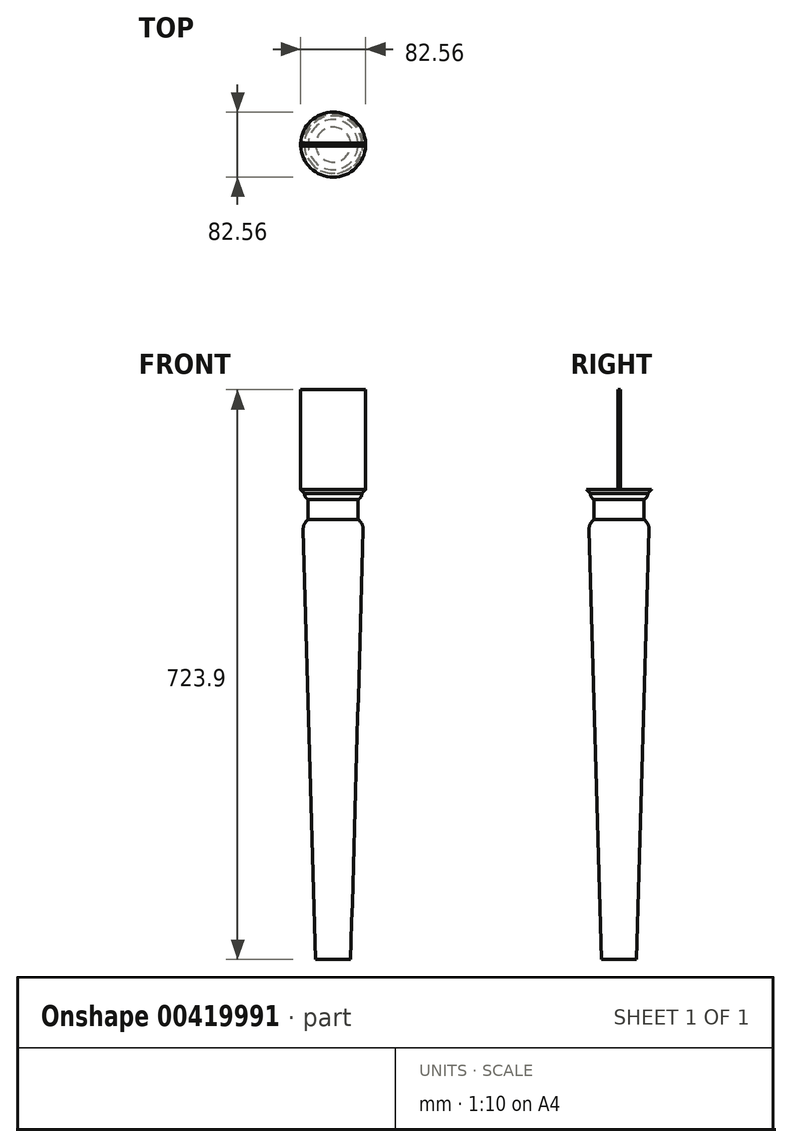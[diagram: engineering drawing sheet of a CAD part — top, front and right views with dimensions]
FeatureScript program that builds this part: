
annotation { "Feature Type Name" : "Feature", "Feature Type Description" : "" }
export const myFeature = defineFeature(function(context is Context, id is Id, definition is map)
    precondition{}
    {
        {
            assignVariable(context, id + "F0", {"name" : "squareSize", "anyValue" : 3.25});
        }
        {
            var Q0;
            Q0=qCreatedBy(makeId("Front.planeOp"),FACE);
            var sketch = newSketch(context, id + "F1", { "sketchPlane" : qUnion([Q0])});
            skLineSegment(sketch, "E0", {"start": v(0, 0) * mm, "end": v(0, -723.9) * mm});
            skLineSegment(sketch, "E1", {"start": v(0, 0) * mm, "end": v(41.27, 0) * mm});
            skLineSegment(sketch, "E2", {"start": v(41.27, 0) * mm, "end": v(41.28, -127) * mm});
            skLineSegment(sketch, "E3", {"start": v(22.23, -723.9) * mm, "end": v(38.1, -177.8) * mm});
            skLineSegment(sketch, "E4", {"start": v(41.27, -127) * mm, "end": v(0, -127) * mm});
            skLineSegment(sketch, "E5", {"start": v(41.28, -127) * mm, "end": v(41.28, -723.9) * mm, "construction": true});
            skLineSegment(sketch, "E6.MirrorCS", {"start": v(-41.27, -127) * mm, "end": v(0, -127) * mm});
            skLineSegment(sketch, "E7.MirrorCS", {"start": v(-41.27, 0) * mm, "end": v(-41.28, -127) * mm});
            skLineSegment(sketch, "E8.MirrorCS", {"start": v(0, 0) * mm, "end": v(-41.27, 0) * mm});
            skLineSegment(sketch, "E9", {"start": v(31.75, -139.7) * mm, "end": v(31.75, -165.1) * mm});
            skArc(sketch, "E10", {"start": v(36.51, -131.76) * mm, "mid": v(53.34, -112.03) * mm, "end": v(65.6, -89.16) * mm});
            skArc(sketch, "E11", {"start": v(31.75, -139.7) * mm, "mid": v(35.23, -136.4) * mm, "end": v(36.51, -131.76) * mm});
            skArc(sketch, "E12", {"start": v(38.1, -177.8) * mm, "mid": v(36.52, -170.65) * mm, "end": v(31.75, -165.1) * mm});
            skLineSegment(sketch, "E13", {"start": v(22.23, -723.9) * mm, "end": v(0, -723.9) * mm});
            skLineSegment(sketch, "E14", {"start": v(-41.27, -89.16) * mm, "end": v(65.6, -89.16) * mm});
            skPoint(sketch, "E15.orphan", {"position": v(0, -89.16) * mm});
            skSolve(sketch);
        }
        {
            var Q0;
            Q0=makeQuery(id+"F1.imprint","IMPRINT",FACE,{"disambiguationData":[TD([[makeQuery(id+"F1.imprint","IMPRINT",EDGE,{"derivedFrom":sQuery(id+"F1.wireOp",EDGE,"E1")}),-1.0]])]});
            var Q1;
            {var subQ2=sQuery(id+"F1.wireOp",EDGE,"E6.MirrorCS");Q1=makeQuery(id+"F1.imprint","IMPRINT",FACE,{"disambiguationData":[TD([[makeQuery(id+"F1.imprint","IMPRINT",EDGE,{"derivedFrom":subQ2}),1.0]])]});}
            var Q2;
            {var subQ0=sQuery(id+"F1.wireOp",EDGE,"E4");Q2=makeQuery(id+"F1.imprint","IMPRINT",FACE,{"disambiguationData":[TD([[makeQuery(id+"F1.imprint","IMPRINT",EDGE,{"derivedFrom":subQ0}),-1.0]])]});}
            extrude(context, id + "F2", {"entities" : qUnion([Q0, Q1, Q2]), "endBound" : BoundingType.SYMMETRIC, "depth" : (getVariable(context, 'squareSize')) * mm});
        }
        {
            var Q0;
            Q0=makeQuery(id+"F1.imprint","IMPRINT",FACE,{"disambiguationData":[TD([[makeQuery(id+"F1.imprint","IMPRINT",EDGE,{"derivedFrom":sQuery(id+"F1.wireOp",EDGE,"E3")}),1.0]])]});
            var Q1;
            {var subQ0=sQuery(id+"F1.wireOp",EDGE,"E4");Q1=makeQuery(id+"F1.imprint","IMPRINT",FACE,{"disambiguationData":[TD([[makeQuery(id+"F1.imprint","IMPRINT",EDGE,{"derivedFrom":subQ0}),-1.0]])]});}
            var Q2;
            {var subQ0=sQuery(id+"F1.wireOp",EDGE,"E10");var subQ3=sQuery(id+"F1.wireOp",EDGE,"E14");var subQ5=makeQuery(id+"F1.imprint","INTERSECT",VERTEX,{"derivedFrom":[subQ0,subQ3]});Q2=makeQuery(id+"F1.imprint","IMPRINT",FACE,{"disambiguationData":[TD([[makeQuery(id+"F1.imprint","IMPRINT",EDGE,{"disambiguationData":[TD([[subQ5,1.0]])],"derivedFrom":subQ3}),-1.0]])]});}
            var Q3;
            Q3=sQuery(id+"F1.wireOp",EDGE,"E0");
            revolve(context, id + "F3", {"operationType" : NewBodyOperationType.INTERSECT, "entities" : qUnion([Q0, Q1, Q2]), "axis" : qUnion([Q3]), "revolveType" : RevolveType.FULL});
        }
        {
            var Q0;
            {var subQ0=sQuery(id+"F1.wireOp",EDGE,"E8.MirrorCS");Q0=makeQuery(id+"F1.imprint","IMPRINT",FACE,{"disambiguationData":[TD([[makeQuery(id+"F1.imprint","IMPRINT",EDGE,{"derivedFrom":subQ0}),1.0]])]});}
            var Q1;
            {var subQ0=sQuery(id+"F1.wireOp",EDGE,"E1");Q1=makeQuery(id+"F1.imprint","IMPRINT",FACE,{"disambiguationData":[TD([[makeQuery(id+"F1.imprint","IMPRINT",EDGE,{"derivedFrom":subQ0}),-1.0]])]});}
            extrude(context, id + "F4", {"entities" : qUnion([Q0, Q1]), "operationType" : NewBodyOperationType.ADD, "endBound" : BoundingType.SYMMETRIC, "depth" : (getVariable(context, 'squareSize')) * mm});
        }
        {
            var Q0;
            Q0=makeQuery(id+"F1.imprint","IMPRINT",FACE,{"disambiguationData":[TD([[makeQuery(id+"F1.imprint","IMPRINT",EDGE,{"derivedFrom":sQuery(id+"F1.wireOp",EDGE,"E3")}),1.0]])]});
            var Q1;
            Q1=sQuery(id+"F1.wireOp",EDGE,"E0");
            revolve(context, id + "F5", {"operationType" : NewBodyOperationType.ADD, "entities" : qUnion([Q0]), "axis" : qUnion([Q1]), "revolveType" : RevolveType.FULL});
        }
    });
